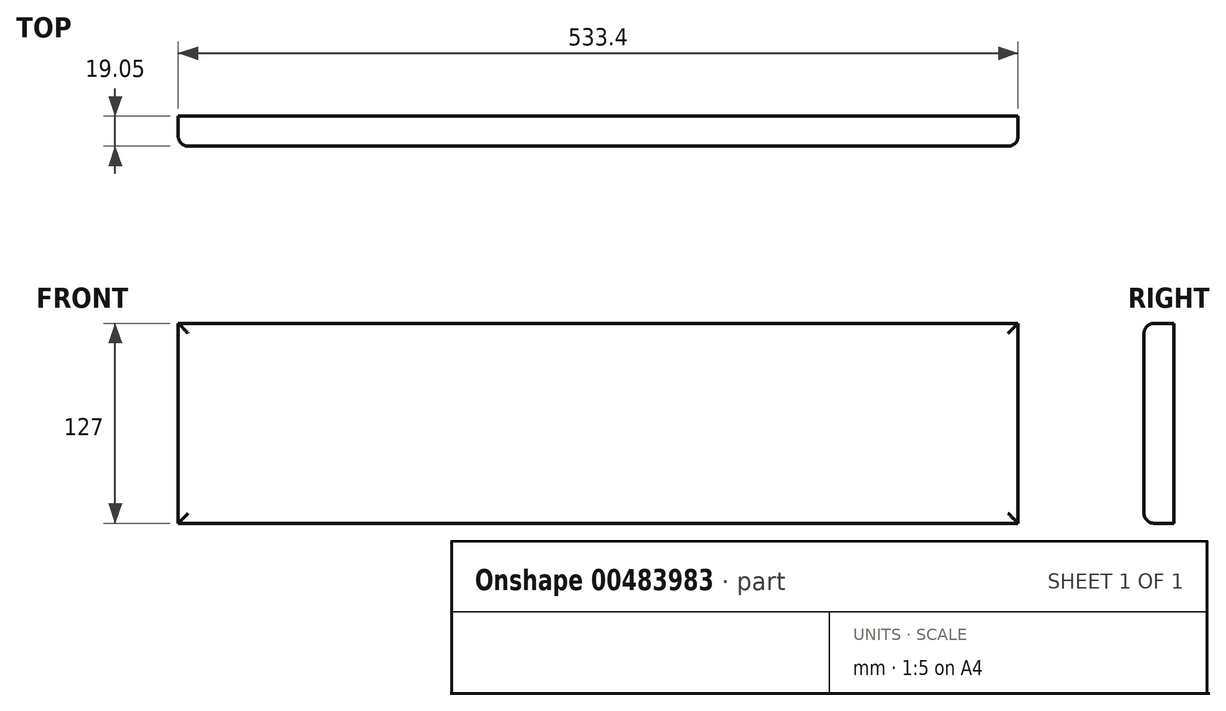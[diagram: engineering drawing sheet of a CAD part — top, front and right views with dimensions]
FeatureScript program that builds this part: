
annotation { "Feature Type Name" : "Feature", "Feature Type Description" : "" }
export const myFeature = defineFeature(function(context is Context, id is Id, definition is map)
    precondition{}
    {
        {
            var Q0;
            Q0=qCreatedBy(makeId("Front.planeOp"),FACE);
            var sketch = newSketch(context, id + "F0", { "sketchPlane" : qUnion([Q0])});
            skLineSegment(sketch, "E0.bottom", {"start": v(266.7, -63.5) * mm, "end": v(-266.7, -63.5) * mm});
            skLineSegment(sketch, "E0.top", {"start": v(266.7, 63.5) * mm, "end": v(-266.7, 63.5) * mm});
            skLineSegment(sketch, "E0.left", {"start": v(266.7, -63.5) * mm, "end": v(266.7, 63.5) * mm});
            skLineSegment(sketch, "E0.right", {"start": v(-266.7, -63.5) * mm, "end": v(-266.7, 63.5) * mm});
            skPoint(sketch, "E0.middle", {"position": v(0, 0) * mm});
            skSolve(sketch);
        }
        {
            var Q0;
            Q0 = qSketchRegion(id + "F0", true);
            extrude(context, id + "F1", {"entities" : qUnion([Q0]), "depth" : 19.05 * mm});
        }
        {
            var Q0;
            Q0=makeQuery(id+"F1.opExtrude","CAP_EDGE",EDGE,{"disambiguationData":[OSD([sQuery(id+"F0.wireOp",EDGE,"E0.top")])],"isStart":false});
            var Q1;
            Q1=makeQuery(id+"F1.opExtrude","CAP_EDGE",EDGE,{"disambiguationData":[OSD([sQuery(id+"F0.wireOp",EDGE,"E0.right")])],"isStart":false});
            var Q2;
            Q2=makeQuery(id+"F1.opExtrude","CAP_EDGE",EDGE,{"disambiguationData":[OSD([sQuery(id+"F0.wireOp",EDGE,"E0.bottom")])],"isStart":false});
            var Q3;
            Q3=makeQuery(id+"F1.opExtrude","CAP_EDGE",EDGE,{"disambiguationData":[OSD([sQuery(id+"F0.wireOp",EDGE,"E0.left")])],"isStart":false});
            fillet(context, id + "F2", {"entities" : qUnion([Q0, Q1, Q2, Q3]), "radius" : 6.35 * mm, "tangentPropagation" : true, "allowEdgeOverflow" : false});
        }
    });
